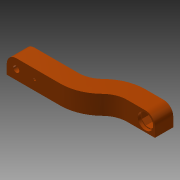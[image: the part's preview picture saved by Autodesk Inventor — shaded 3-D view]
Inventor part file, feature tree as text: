
AUTODESK INVENTOR PART (.ipt)
format: ipt  version: 2013 (Build 170138000, 138)  size: 173,568 bytes
history: native  units: mm
features: extrude x9, sketch x9
ambient origin geometry x8: Origin, YZ Plane, XZ Plane, XY Plane, X Axis, Y Axis, Z Axis, Center Point
bodies: Solid1 (feature_tree)
feature tree (18):
  extrude  "Extrusion1"  Depth=60.0mm
  extrude  "Extrusion2"  Depth=150.0mm
  extrude  "Extrusion3"  Depth=26.0mm TaperAngle=0.0deg
  extrude  "Extrusion4"  Depth=26.0mm TaperAngle=0.0deg
  extrude  "Extrusion5"  Depth=8.2mm
  extrude  "Extrusion6"  Depth=3.0mm
  extrude  "Extrusion7"  Depth=26.0mm TaperAngle=0.0deg
  extrude  "Extrusion8"  Depth=15.0mm
  extrude  "Extrusion9"  Depth=26.0mm TaperAngle=0.0deg
  sketch  "Sketch1"  dims[d0=25.0mm d1=60.0mm]
  sketch  "Sketch2"  dims[d2=25.0mm d3=150.0mm]
  sketch  "Sketch3"  dims[d4=1.5mm d5=26.0mm d6=0.0mm]
  sketch  "Sketch4"  dims[d7=26.0mm d8=0.0mm d9=26.0mm d10=0.0mm]
  sketch  "Sketch5"  dims[d11=26.0mm d12=0.0mm d13=8.2mm]
  sketch  "Sketch6"  dims[d15=26.0mm d16=0.0mm d17=3.0mm]
  sketch  "Sketch7"  dims[d19=25.0mm d20=26.0mm d21=0.0mm]
  sketch  "Sketch8"  dims[d22=21.0mm d24=15.0mm]
  sketch  "Sketch9"  dims[d25=18.0mm d26=26.0mm d27=0.0mm d28=21.1mm d30=4.0mm d31=0.0mm d32=4.0mm d33=0.0mm]
